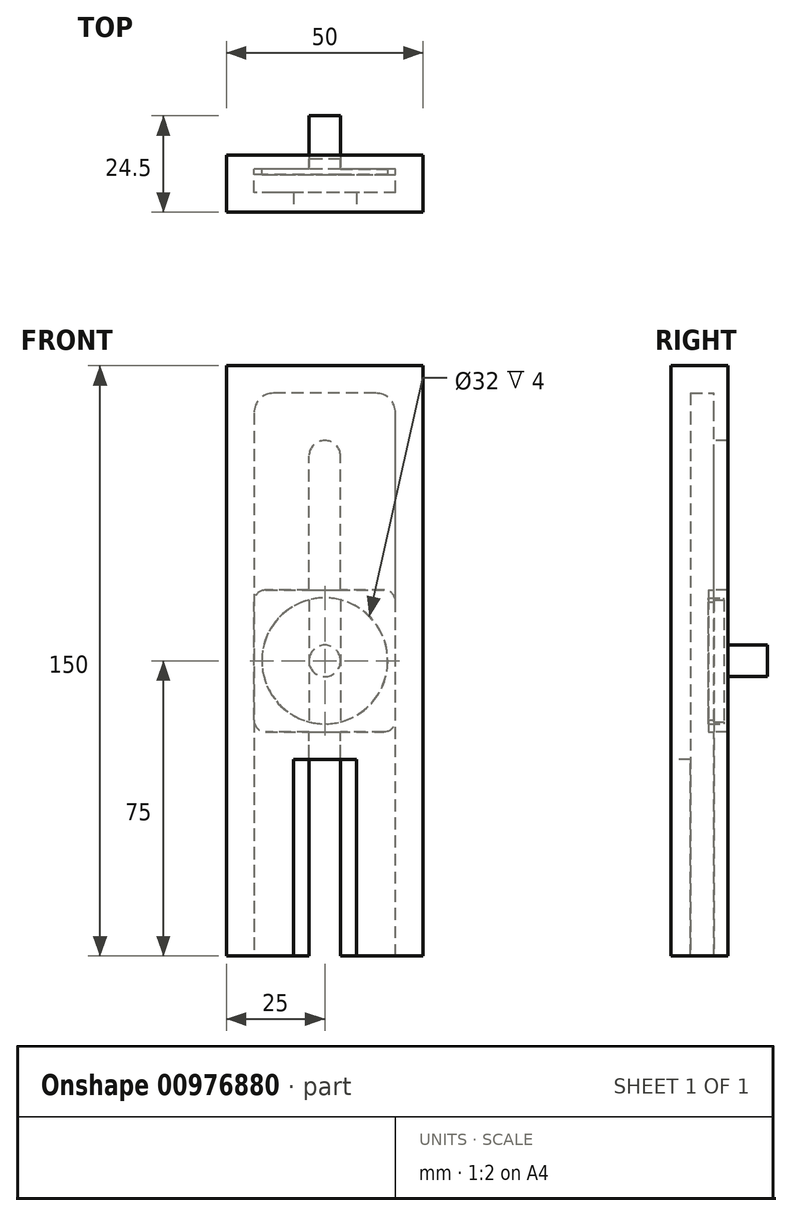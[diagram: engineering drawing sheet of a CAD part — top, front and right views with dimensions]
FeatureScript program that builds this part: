
annotation { "Feature Type Name" : "Feature", "Feature Type Description" : "" }
export const myFeature = defineFeature(function(context is Context, id is Id, definition is map)
    precondition{}
    {
        {
            var Q0;
            Q0=qCreatedBy(makeId("Front.planeOp"),FACE);
            var sketch = newSketch(context, id + "F0", { "sketchPlane" : qUnion([Q0])});
            skLineSegment(sketch, "E0.bottom", {"start": v(25, -75) * mm, "end": v(-25, -75) * mm});
            skLineSegment(sketch, "E0.top", {"start": v(25, 75) * mm, "end": v(-25, 75) * mm});
            skLineSegment(sketch, "E0.left", {"start": v(25, -75) * mm, "end": v(25, 75) * mm});
            skLineSegment(sketch, "E0.right", {"start": v(-25, -75) * mm, "end": v(-25, 75) * mm});
            skPoint(sketch, "E0.middle", {"position": v(0, 0) * mm});
            skSolve(sketch);
        }
        {
            var Q0;
            Q0=makeQuery(id+"F0.imprint","IMPRINT",FACE,{"disambiguationData":[TD([[makeQuery(id+"F0.imprint","IMPRINT",EDGE,{"derivedFrom":sQuery(id+"F0.wireOp",EDGE,"E0.bottom")}),-1.0]])]});
            extrude(context, id + "F1", {"entities" : qUnion([Q0]), "depth" : 3.5 * mm, "offsetDistance" : 25 * mm});
        }
        {
            var Q0;
            Q0=makeQuery(id+"F1.opExtrude","CAP_FACE",FACE,{"disambiguationData":[OSD([sQuery(id+"F0.wireOp",EDGE,"E0.bottom"),sQuery(id+"F0.wireOp",EDGE,"E0.top"),sQuery(id+"F0.wireOp",EDGE,"E0.left"),sQuery(id+"F0.wireOp",EDGE,"E0.right")])],"isStart":false});
            var sketch = newSketch(context, id + "F2", { "sketchPlane" : qUnion([Q0])});
            skLineSegment(sketch, "E1.top", {"start": v(13, 68) * mm, "end": v(-13, 68) * mm});
            skLineSegment(sketch, "E1.left", {"start": v(18, -68) * mm, "end": v(18, 63) * mm});
            skLineSegment(sketch, "E1.right", {"start": v(-18, -68) * mm, "end": v(-18, 63) * mm});
            skPoint(sketch, "E1.middle", {"position": v(0, 0) * mm});
            skLineSegment(sketch, "E2", {"start": v(18, -68) * mm, "end": v(18, -75) * mm});
            skLineSegment(sketch, "E3", {"start": v(-18, -68) * mm, "end": v(-18, -75) * mm});
            skLineSegment(sketch, "E4.bottom", {"start": v(-4, -75) * mm, "end": v(4, -75) * mm});
            skLineSegment(sketch, "E4.top", {"start": v(0, 56) * mm, "end": v(0, 56) * mm});
            skLineSegment(sketch, "E4.left", {"start": v(-4, -75) * mm, "end": v(-4, 52) * mm});
            skLineSegment(sketch, "E4.right", {"start": v(4, -75) * mm, "end": v(4, 52) * mm});
            skPoint(sketch, "E5.visualSharp", {"position": v(-18, 68) * mm});
            skArc(sketch, "E5.filletArc", {"start": v(-13, 68) * mm, "mid": v(-16.54, 66.54) * mm, "end": v(-18, 63) * mm});
            skPoint(sketch, "E6.visualSharp", {"position": v(18, 68) * mm});
            skArc(sketch, "E6.filletArc", {"start": v(18, 63) * mm, "mid": v(16.54, 66.54) * mm, "end": v(13, 68) * mm});
            skPoint(sketch, "E7.visualSharp", {"position": v(-4, 56) * mm});
            skArc(sketch, "E7.filletArc", {"start": v(0, 56) * mm, "mid": v(-2.83, 54.83) * mm, "end": v(-4, 52) * mm});
            skPoint(sketch, "E8.visualSharp", {"position": v(4, 56) * mm});
            skArc(sketch, "E8.filletArc", {"start": v(4, 52) * mm, "mid": v(2.83, 54.83) * mm, "end": v(0, 56) * mm});
            skSolve(sketch);
        }
        {
            var Q0;
            Q0=makeQuery(id+"F2.imprint","IMPRINT",FACE,{"disambiguationData":[TD([[makeQuery(id+"F2.imprint","IMPRINT",EDGE,{"derivedFrom":sQuery(id+"F2.wireOp",EDGE,"E1.top")}),-1.0]])]});
            extrude(context, id + "F3", {"entities" : qUnion([Q0]), "operationType" : NewBodyOperationType.ADD, "depth" : 6 * mm, "offsetDistance" : 25 * mm});
        }
        {
            var Q0;
            Q0=makeQuery(id+"F2.imprint","IMPRINT",FACE,{"disambiguationData":[TD([[makeQuery(id+"F2.imprint","IMPRINT",EDGE,{"derivedFrom":sQuery(id+"F2.wireOp",EDGE,"E4.bottom")}),-1.0]])]});
            extrude(context, id + "F4", {"entities" : qUnion([Q0]), "operationType" : NewBodyOperationType.REMOVE, "oppositeDirection" : true, "depth" : 25 * mm, "offsetDistance" : 25 * mm});
        }
        {
            var Q0;
            Q0=makeQuery(id+"F3.opExtrude","CAP_FACE",FACE,{"disambiguationData":[OSD([sQuery(id+"F0.wireOp",EDGE,"E0.bottom"),sQuery(id+"F0.wireOp",EDGE,"E0.top"),sQuery(id+"F0.wireOp",EDGE,"E0.left"),sQuery(id+"F0.wireOp",EDGE,"E0.right"),sQuery(id+"F2.wireOp",EDGE,"E1.top"),sQuery(id+"F2.wireOp",EDGE,"E1.left"),sQuery(id+"F2.wireOp",EDGE,"E1.right"),sQuery(id+"F2.wireOp",EDGE,"E2"),sQuery(id+"F2.wireOp",EDGE,"E3"),sQuery(id+"F2.wireOp",EDGE,"E5.filletArc"),sQuery(id+"F2.wireOp",EDGE,"E6.filletArc")])],"isStart":false});
            var sketch = newSketch(context, id + "F5", { "sketchPlane" : qUnion([Q0])});
            skLineSegment(sketch, "E9.bottom", {"start": v(-25, 75) * mm, "end": v(25, 75) * mm});
            skLineSegment(sketch, "E9.top", {"start": v(-25, -75) * mm, "end": v(25, -75) * mm});
            skLineSegment(sketch, "E9.left", {"start": v(-25, 75) * mm, "end": v(-25, -75) * mm});
            skLineSegment(sketch, "E9.right", {"start": v(25, 75) * mm, "end": v(25, -75) * mm});
            skSolve(sketch);
        }
        {
            var Q0;
            Q0 = qSketchRegion(id + "F5", true);
            extrude(context, id + "F6", {"entities" : qUnion([Q0]), "operationType" : NewBodyOperationType.ADD, "depth" : 5 * mm, "offsetDistance" : 25 * mm});
        }
        {
            var Q0;
            Q0=qCreatedBy(makeId("Front.planeOp"),FACE);
            var sketch = newSketch(context, id + "F7", { "sketchPlane" : qUnion([Q0])});
            skLineSegment(sketch, "E10.bottom", {"start": v(-15, -18) * mm, "end": v(15, -18) * mm});
            skLineSegment(sketch, "E10.top", {"start": v(-15, 18) * mm, "end": v(15, 18) * mm});
            skLineSegment(sketch, "E10.left", {"start": v(-18, -15) * mm, "end": v(-18, 15) * mm});
            skLineSegment(sketch, "E10.right", {"start": v(18, -15) * mm, "end": v(18, 15) * mm});
            skPoint(sketch, "E10.middle", {"position": v(0, 0) * mm});
            skPoint(sketch, "E11.visualSharp", {"position": v(18, 18) * mm});
            skArc(sketch, "E11.filletArc", {"start": v(18, 15) * mm, "mid": v(17.12, 17.12) * mm, "end": v(15, 18) * mm});
            skPoint(sketch, "E12.visualSharp", {"position": v(-18, 18) * mm});
            skArc(sketch, "E12.filletArc", {"start": v(-15, 18) * mm, "mid": v(-17.12, 17.12) * mm, "end": v(-18, 15) * mm});
            skPoint(sketch, "E13.visualSharp", {"position": v(-18, -18) * mm});
            skArc(sketch, "E13.filletArc", {"start": v(-18, -15) * mm, "mid": v(-17.12, -17.12) * mm, "end": v(-15, -18) * mm});
            skPoint(sketch, "E14.visualSharp", {"position": v(18, -18) * mm});
            skArc(sketch, "E14.filletArc", {"start": v(15, -18) * mm, "mid": v(17.12, -17.12) * mm, "end": v(18, -15) * mm});
            skCircle(sketch, "E15", {"center": v(0, 0) * mm, "radius": 16 * mm});
            skCircle(sketch, "E16", {"center": v(0, 0) * mm, "radius": 4 * mm});
            skSolve(sketch);
        }
        {
            var Q0;
            Q0=makeQuery(id+"F7.imprint","IMPRINT",FACE,{"disambiguationData":[TD([[makeQuery(id+"F7.imprint","IMPRINT",EDGE,{"derivedFrom":sQuery(id+"F7.wireOp",EDGE,"E10.bottom")}),1.0]])]});
            var Q1;
            Q1=makeQuery(id+"F7.imprint","IMPRINT",FACE,{"disambiguationData":[TD([[makeQuery(id+"F7.imprint","IMPRINT",EDGE,{"derivedFrom":sQuery(id+"F7.wireOp",EDGE,"E15")}),1.0]])]});
            var Q2;
            Q2=makeQuery(id+"F7.imprint","IMPRINT",FACE,{"disambiguationData":[TD([[makeQuery(id+"F7.imprint","IMPRINT",EDGE,{"derivedFrom":sQuery(id+"F7.wireOp",EDGE,"E16")}),1.0]])]});
            extrude(context, id + "F8", {"entities" : qUnion([Q0, Q1, Q2]), "depth" : 1 * mm, "offsetDistance" : 25 * mm});
        }
        {
            var Q0;
            Q0=makeQuery(id+"F7.imprint","IMPRINT",FACE,{"disambiguationData":[TD([[makeQuery(id+"F7.imprint","IMPRINT",EDGE,{"derivedFrom":sQuery(id+"F7.wireOp",EDGE,"E10.bottom")}),1.0]])]});
            extrude(context, id + "F9", {"entities" : qUnion([Q0]), "operationType" : NewBodyOperationType.ADD, "depth" : 5 * mm, "offsetDistance" : 25 * mm});
        }
        {
            var Q0;
            Q0=makeQuery(id+"F7.imprint","IMPRINT",FACE,{"disambiguationData":[TD([[makeQuery(id+"F7.imprint","IMPRINT",EDGE,{"derivedFrom":sQuery(id+"F7.wireOp",EDGE,"E16")}),1.0]])]});
            extrude(context, id + "F10", {"entities" : qUnion([Q0]), "operationType" : NewBodyOperationType.ADD, "oppositeDirection" : true, "depth" : 10 * mm, "offsetDistance" : 25 * mm});
        }
        {
            var Q0;
            Q0=makeQuery(id+"F6.opExtrude","CAP_FACE",FACE,{"disambiguationData":[OSD([sQuery(id+"F5.wireOp",EDGE,"E9.bottom"),sQuery(id+"F5.wireOp",EDGE,"E9.top"),sQuery(id+"F5.wireOp",EDGE,"E9.left"),sQuery(id+"F5.wireOp",EDGE,"E9.right")])],"isStart":false});
            var sketch = newSketch(context, id + "F11", { "sketchPlane" : qUnion([Q0])});
            skLineSegment(sketch, "E17.bottom", {"start": v(8, -75) * mm, "end": v(-8, -75) * mm});
            skLineSegment(sketch, "E17.top", {"start": v(8, -25) * mm, "end": v(-8, -25) * mm});
            skLineSegment(sketch, "E17.left", {"start": v(8, -75) * mm, "end": v(8, -25) * mm});
            skLineSegment(sketch, "E17.right", {"start": v(-8, -75) * mm, "end": v(-8, -25) * mm});
            skSolve(sketch);
        }
        {
            var Q0;
            Q0=makeQuery(id+"F11.imprint","IMPRINT",FACE,{"disambiguationData":[TD([[makeQuery(id+"F11.imprint","IMPRINT",EDGE,{"derivedFrom":sQuery(id+"F11.wireOp",EDGE,"E17.bottom")}),-1.0]])]});
            extrude(context, id + "F12", {"entities" : qUnion([Q0]), "operationType" : NewBodyOperationType.REMOVE, "oppositeDirection" : true, "depth" : 6.1 * mm, "offsetDistance" : 25 * mm});
        }
    });
